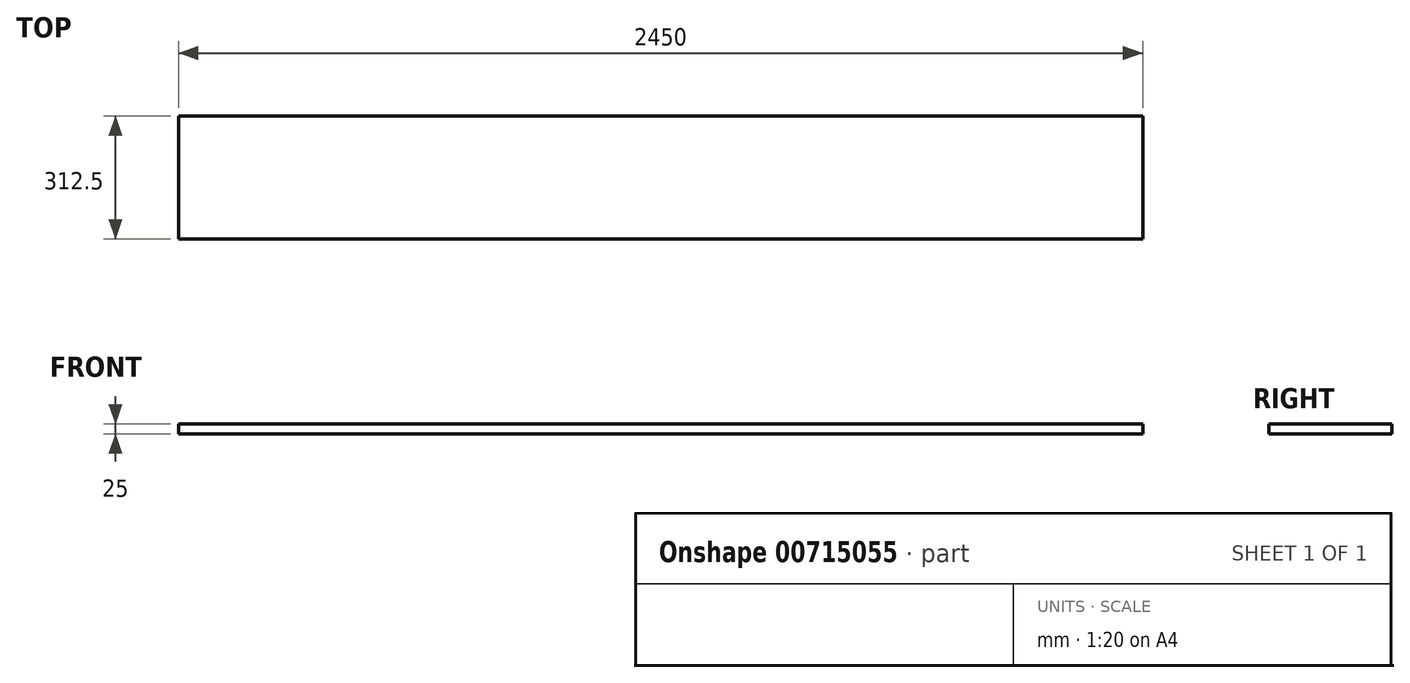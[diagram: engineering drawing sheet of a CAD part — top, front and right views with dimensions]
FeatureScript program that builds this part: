
annotation { "Feature Type Name" : "Feature", "Feature Type Description" : "" }
export const myFeature = defineFeature(function(context is Context, id is Id, definition is map)
    precondition{}
    {
        {
            var Q0;
            Q0=qCreatedBy(makeId("Top.planeOp"),FACE);
            var sketch = newSketch(context, id + "F0", { "sketchPlane" : qUnion([Q0])});
            skLineSegment(sketch, "E0.bottom", {"start": v(1225, 156.25) * mm, "end": v(-1225, 156.25) * mm});
            skLineSegment(sketch, "E0.top", {"start": v(1225, -156.25) * mm, "end": v(-1225, -156.25) * mm});
            skLineSegment(sketch, "E0.left", {"start": v(1225, 156.25) * mm, "end": v(1225, -156.25) * mm});
            skLineSegment(sketch, "E0.right", {"start": v(-1225, 156.25) * mm, "end": v(-1225, -156.25) * mm});
            skPoint(sketch, "E0.middle", {"position": v(0, 0) * mm});
            skSolve(sketch);
        }
        {
            var Q0;
            Q0=makeQuery(id+"F0.imprint","IMPRINT",FACE,{"disambiguationData":[TD([[makeQuery(id+"F0.imprint","IMPRINT",EDGE,{"derivedFrom":sQuery(id+"F0.wireOp",EDGE,"E0.bottom")}),1.0]])]});
            extrude(context, id + "F1", {"entities" : qUnion([Q0]), "depth" : 25 * mm, "offsetDistance" : 25 * mm});
        }
    });
